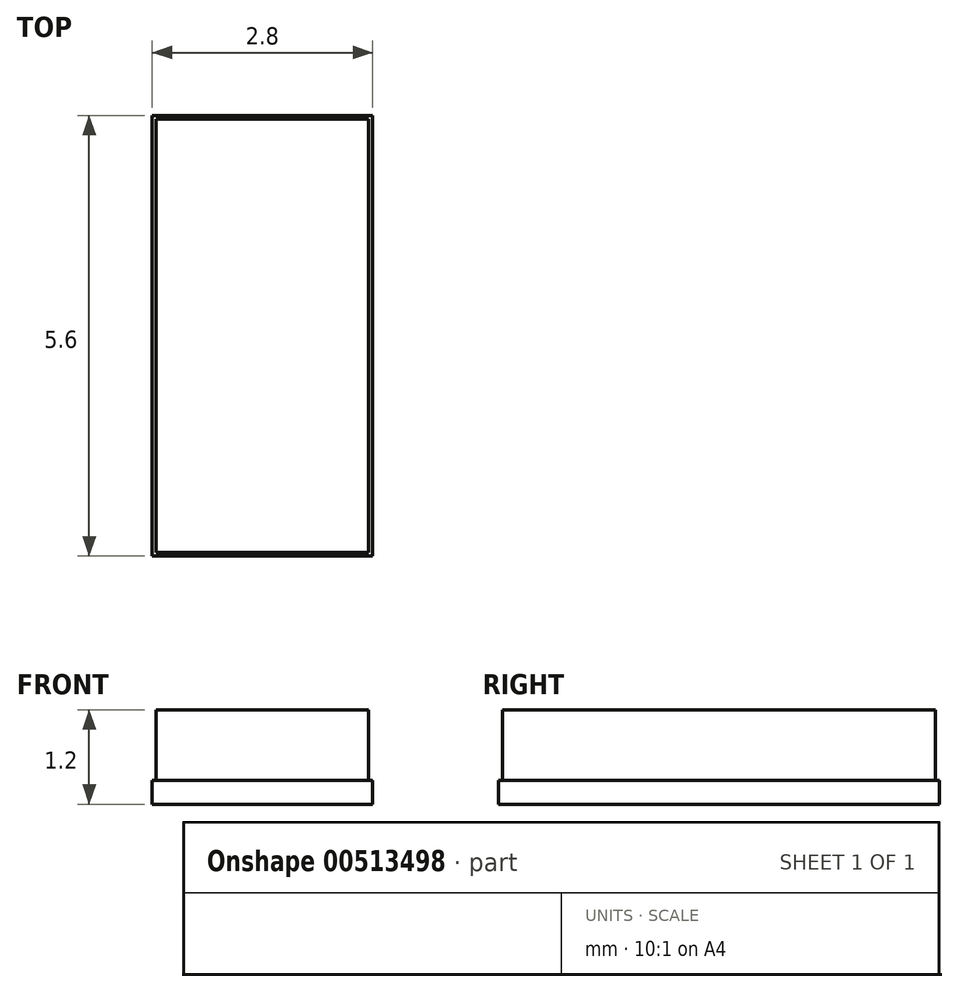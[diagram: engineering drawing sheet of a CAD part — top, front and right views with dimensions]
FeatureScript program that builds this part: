
annotation { "Feature Type Name" : "Feature", "Feature Type Description" : "" }
export const myFeature = defineFeature(function(context is Context, id is Id, definition is map)
    precondition{}
    {
        {
            var Q0;
            Q0=qCreatedBy(makeId("Top.planeOp"),FACE);
            var sketch = newSketch(context, id + "F0", { "sketchPlane" : qUnion([Q0])});
            skLineSegment(sketch, "E0.bottom", {"start": v(1.4, -2.8) * mm, "end": v(-1.4, -2.8) * mm});
            skLineSegment(sketch, "E0.top", {"start": v(1.4, 2.8) * mm, "end": v(-1.4, 2.8) * mm});
            skLineSegment(sketch, "E0.left", {"start": v(1.4, -2.8) * mm, "end": v(1.4, 2.8) * mm});
            skLineSegment(sketch, "E0.right", {"start": v(-1.4, -2.8) * mm, "end": v(-1.4, 2.8) * mm});
            skPoint(sketch, "E0.middle", {"position": v(0, 0) * mm});
            skSolve(sketch);
        }
        {
            var Q0;
            Q0=makeQuery(id+"F0.imprint","IMPRINT",FACE,{"disambiguationData":[TD([[makeQuery(id+"F0.imprint","IMPRINT",EDGE,{"derivedFrom":sQuery(id+"F0.wireOp",EDGE,"E0.bottom")}),-1.0]])]});
            extrude(context, id + "F1", {"entities" : qUnion([Q0]), "depth" : .3 * mm});
        }
        {
            var Q0;
            Q0=makeQuery(id+"F1.opExtrude","CAP_FACE",FACE,{"disambiguationData":[OSD([sQuery(id+"F0.wireOp",EDGE,"E0.bottom"),sQuery(id+"F0.wireOp",EDGE,"E0.top"),sQuery(id+"F0.wireOp",EDGE,"E0.left"),sQuery(id+"F0.wireOp",EDGE,"E0.right")])],"isStart":false});
            var sketch = newSketch(context, id + "F2", { "sketchPlane" : qUnion([Q0])});
            skLineSegment(sketch, "E1.bottom", {"start": v(1.35, -2.75) * mm, "end": v(-1.35, -2.75) * mm});
            skLineSegment(sketch, "E1.top", {"start": v(1.35, 2.75) * mm, "end": v(-1.35, 2.75) * mm});
            skLineSegment(sketch, "E1.left", {"start": v(1.35, -2.75) * mm, "end": v(1.35, 2.75) * mm});
            skLineSegment(sketch, "E1.right", {"start": v(-1.35, -2.75) * mm, "end": v(-1.35, 2.75) * mm});
            skPoint(sketch, "E1.middle", {"position": v(0, 0) * mm});
            skSolve(sketch);
        }
        {
            var Q0;
            Q0=makeQuery(id+"F2.imprint","IMPRINT",FACE,{"disambiguationData":[TD([[makeQuery(id+"F2.imprint","IMPRINT",EDGE,{"derivedFrom":sQuery(id+"F2.wireOp",EDGE,"E1.bottom")}),-1.0]])]});
            extrude(context, id + "F3", {"entities" : qUnion([Q0]), "operationType" : NewBodyOperationType.ADD, "depth" : .9 * mm});
        }
    });
